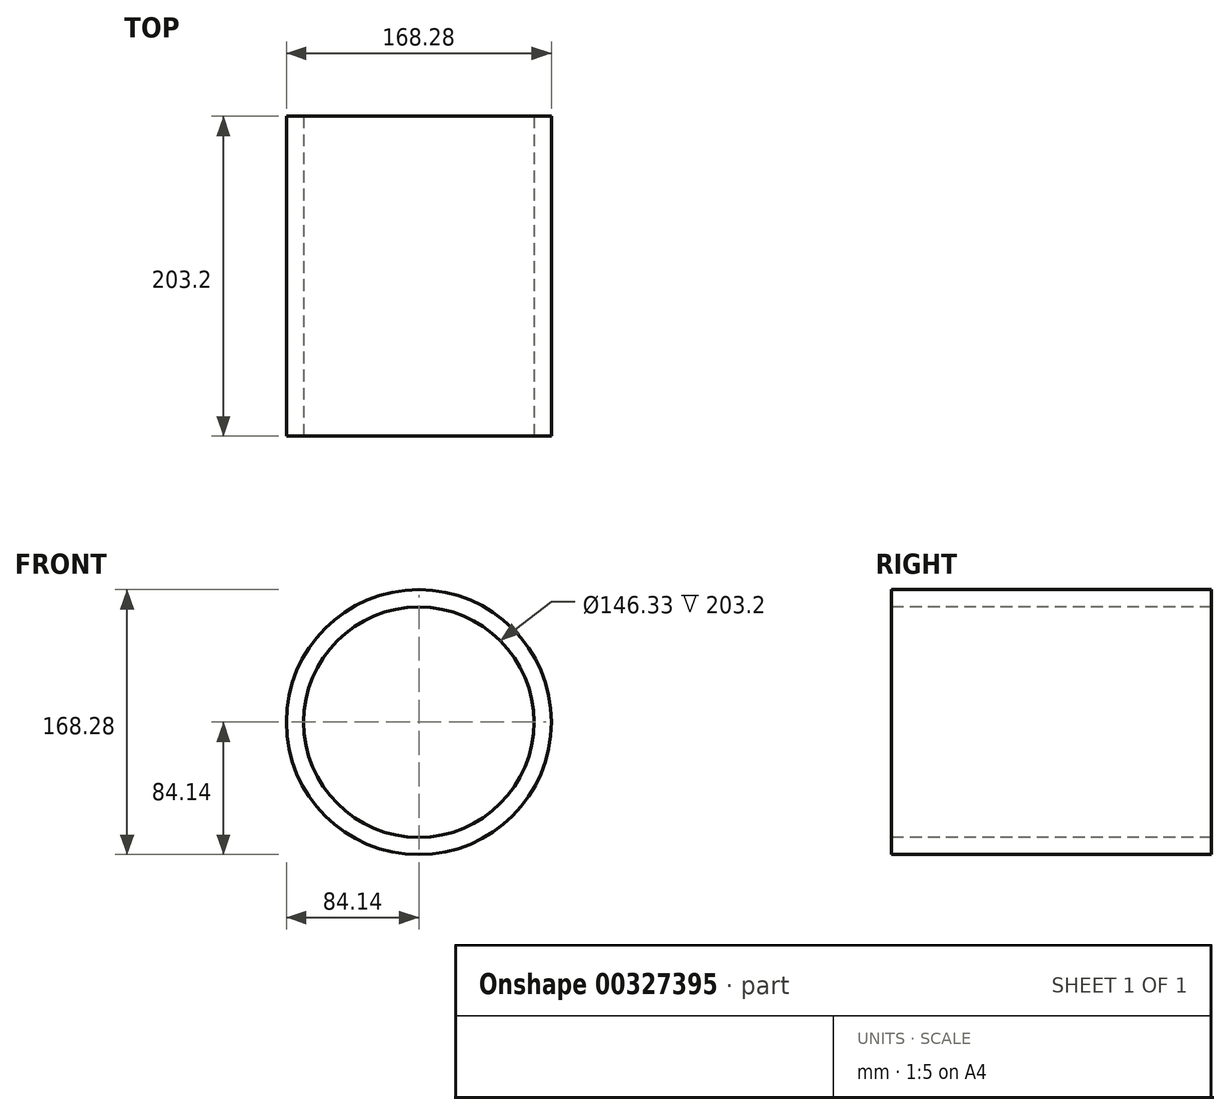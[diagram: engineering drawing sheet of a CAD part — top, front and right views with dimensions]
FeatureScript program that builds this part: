
annotation { "Feature Type Name" : "Feature", "Feature Type Description" : "" }
export const myFeature = defineFeature(function(context is Context, id is Id, definition is map)
    precondition{}
    {
        {
            var Q0;
            Q0=qCreatedBy(makeId("Front.planeOp"), FACE);
            var sketch = newSketch(context, id + "F0", { "sketchPlane" : qUnion([Q0])});
            skCircle(sketch, "E0", {"center": v(0, 0) * mm, "radius": 73.16 * mm});
            skCircle(sketch, "E1", {"center": v(0, 0) * mm, "radius": 84.14 * mm});
            skSolve(sketch);
        }
        {
            var Q0;
            Q0 = qSketchRegion(id + "F0", true);
            extrude(context, id + "F1", {"entities" : qUnion([Q0]), "oppositeDirection" : true, "depth" : 203.2 * mm, "offsetDistance" : 25.4 * mm});
        }
    });
